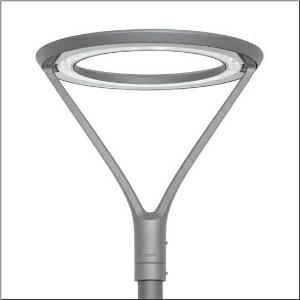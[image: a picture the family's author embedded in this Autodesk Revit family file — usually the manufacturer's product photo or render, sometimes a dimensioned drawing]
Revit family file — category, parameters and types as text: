
# Revit family: dl_r__20_led___st1_2a_5xa51283wa008p_7f17
name_source: partatom
category: Lighting Fixtures
units: mm (PartAtom-declared; Revit-internal decimal feet)

## family parameters
Cut with Voids When Loaded = No
Host = Face
Light Source = No
Part Type = Normal
Room Calculation Point = No
Round Connector Dimension = Use Diameter
Shared = No

## types (1)
- --- (1 x LED 3000K / CRI = 80 (unbekannt), 4180 lm, 3000K)
    Apparent Load = 53 VA
    CIE Flux Codes = 31 69 96 100 100
    Color Rendering = 80
    Color Temperature = 3000K
    Default Elevation = 1800 mm
    Description = DL® 20 LED, mast luminaire, primary light control with reflector, highly specular, primary optical cover: cover, of toughened safety glass of clear glass with excellent transmission level, light distribution: ST1.2a, light emission: direct distribution, primary light characteristic: asymmetric, installation type: post-top, LED High Power LED, rated luminous flux: 4.180 lm, light colour: 830, colour temperature: 3000K, control gear: ECG Plus, control: overheat protection, power reduction, digital communication interface, constant luminous flux control, time-dependent luminous flux control, flexible luminous flux parameterisation, electronic power reduction, mains connection: 220..240V, 50/60Hz, connection cable pre-assembled, cable length: 5 m, start of lifetime: 53 W, end of lifetime: 54 W, reduction: 24 W, luminaire housing, upper part, of cast aluminium, powder-coated, Siteco® metallic grey (DB 702S), diameter: 690 mm, height: 690mm, spigot size: 76mm (post-top), luminaire housing, of cast aluminium, powder-coated, Siteco® metallic grey (DB 702S), protection rating (complete): IP66, insulation class (complete): insulation class II (safety insulation), certification: CE, ENEC, VDE, impact resistance: IK08, permissible ambient temperature for indoor applications: -25..+30°C, standard-compliant lighting for roads and squares, packaging unit: 1 piece

Light Distribution: ST1.2a
    Height = 690 mm
    Lamp = 1 x LED 3000K / CRI >= 80 (unbekannt)
    Lamp Light Flux = 4180 lm
    Lamp count = 1
    Length = 690 mm
    Luminous efficacy = 79 lm/W
    Manufacturer = Siteco
    ModVariant = No
    Model = 5XA51283WA008P
    Number of Poles = 1
    OnlyDefault = Yes
    Power Factor = 1
    Product Name = DL® 20 LED | ST1.2a
    Product group = mast luminaire | pylon top
    ProductGroupID = 6100
    Protection Class = Protection class II
    Protection Degree = IP 66
    RLX_Detail_Level = 1
    RlxData = <blob elided: 206481 chars, md5=e4b90a28>
    Socket = socket
    Standby Power = 0 W
    System Light Flux = 4180 lm
    System Power = 53 W
    Type Comments = factory setting: luminous flux: 100 % | dim-lin: 254 | 683 mA
    Type Image = l_1006001.jpg
    URL = http://relux.com
    VarID = @adj_141385
    Voltage = 0 V
    Weight = 0.00 kg
    Width = 0 mm  [stored 0 ft]

note: [stored X ft] marks values corroborated as IEEE doubles in the binary element streams (Revit-internal decimal feet)

## geometry (parser evidence)
native form markers: Blend x4, Sweep x9
no freeform markers — native parametric forms only
